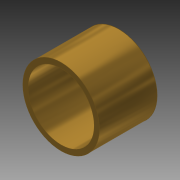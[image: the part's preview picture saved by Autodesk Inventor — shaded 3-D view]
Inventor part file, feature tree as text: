
AUTODESK INVENTOR PART (.ipt)
format: ipt  version: 2014 SP1 (Build 180222100, 222)  size: 87,552 bytes
history: native  units: in
note: dims shown in document units (in); Inventor stores cm internally (conversion verified against a paired STEP export)
features: extrude x1, sketch x1
ambient origin geometry x8: Origin, YZ Plane, XZ Plane, XY Plane, X Axis, Y Axis, Z Axis, Center Point
bodies: Solid1 (feature_tree)
feature tree (2):
  extrude  "Extrusion1"  Depth=0.33in
  sketch  "Sketch1"  dims[d0=0.379in d2=0.437in d3=0.33in d4=0.0in]
